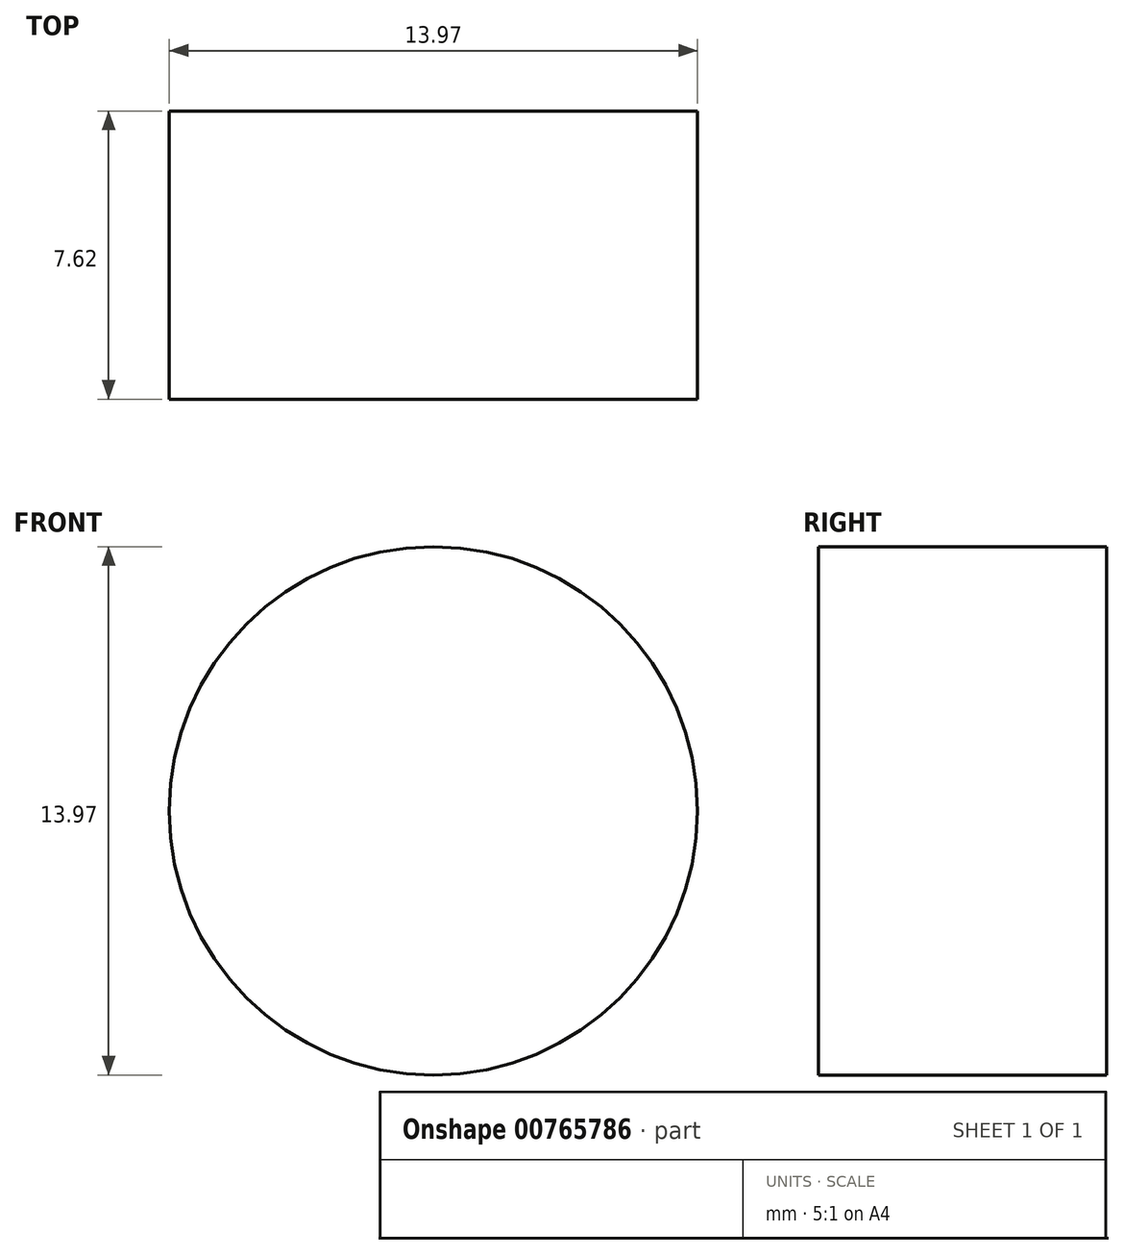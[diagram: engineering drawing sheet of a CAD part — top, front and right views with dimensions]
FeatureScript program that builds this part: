
annotation { "Feature Type Name" : "Feature", "Feature Type Description" : "" }
export const myFeature = defineFeature(function(context is Context, id is Id, definition is map)
    precondition{}
    {
        {
            var Q0;
            Q0=qCreatedBy(makeId("Front.planeOp"),FACE);
            var sketch = newSketch(context, id + "F0", { "sketchPlane" : qUnion([Q0])});
            skCircle(sketch, "E0", {"center": v(-12.02, 0.78) * mm, "radius": 6.99 * mm});
            skSolve(sketch);
        }
        {
            var Q0;
            Q0=makeQuery(id+"F0.imprint","IMPRINT",FACE,{"disambiguationData":[TD([[makeQuery(id+"F0.imprint","IMPRINT",EDGE,{"derivedFrom":sQuery(id+"F0.wireOp",EDGE,"E0")}),1.0]])]});
            extrude(context, id + "F1", {"entities" : qUnion([Q0]), "depth" : 7.62 * mm, "offsetDistance" : 25.4 * mm});
        }
    });
